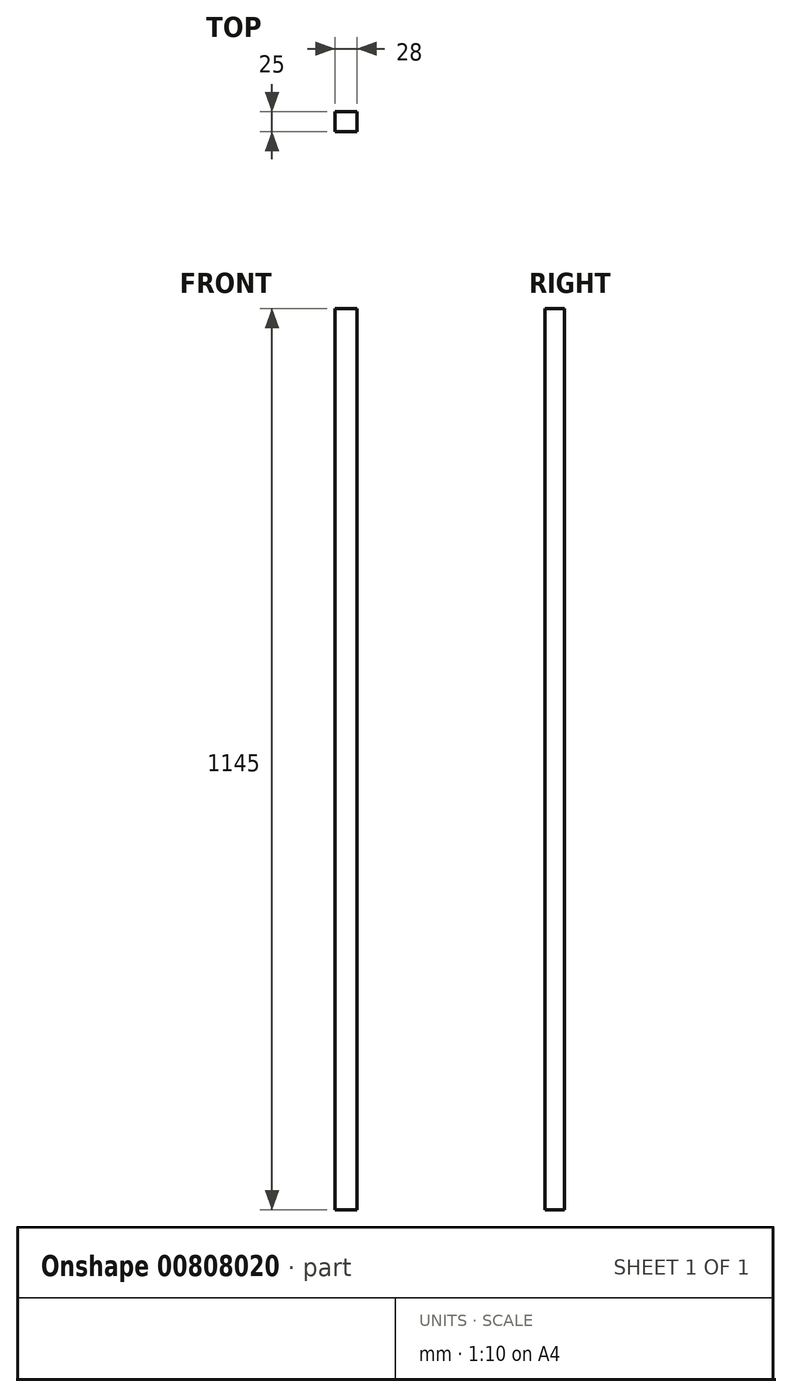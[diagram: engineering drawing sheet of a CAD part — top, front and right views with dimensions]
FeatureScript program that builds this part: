
annotation { "Feature Type Name" : "Feature", "Feature Type Description" : "" }
export const myFeature = defineFeature(function(context is Context, id is Id, definition is map)
    precondition{}
    {
        {
            var Q0;
            Q0=qCreatedBy(makeId("Front.planeOp"),FACE);
            var sketch = newSketch(context, id + "F0", { "sketchPlane" : qUnion([Q0])});
            skLineSegment(sketch, "E0.bottom", {"start": v(-288, 0) * mm, "end": v(-260, 0) * mm});
            skLineSegment(sketch, "E0.top", {"start": v(-288, -1145) * mm, "end": v(-260, -1145) * mm});
            skLineSegment(sketch, "E0.left", {"start": v(-288, 0) * mm, "end": v(-288, -1145) * mm});
            skLineSegment(sketch, "E0.right", {"start": v(-260, 0) * mm, "end": v(-260, -1145) * mm});
            skSolve(sketch);
        }
        {
            var Q0;
            Q0 = qSketchRegion(id + "F0", true);
            extrude(context, id + "F1", {"entities" : qUnion([Q0]), "depth" : 25 * mm, "offsetDistance" : 25 * mm});
        }
    });
